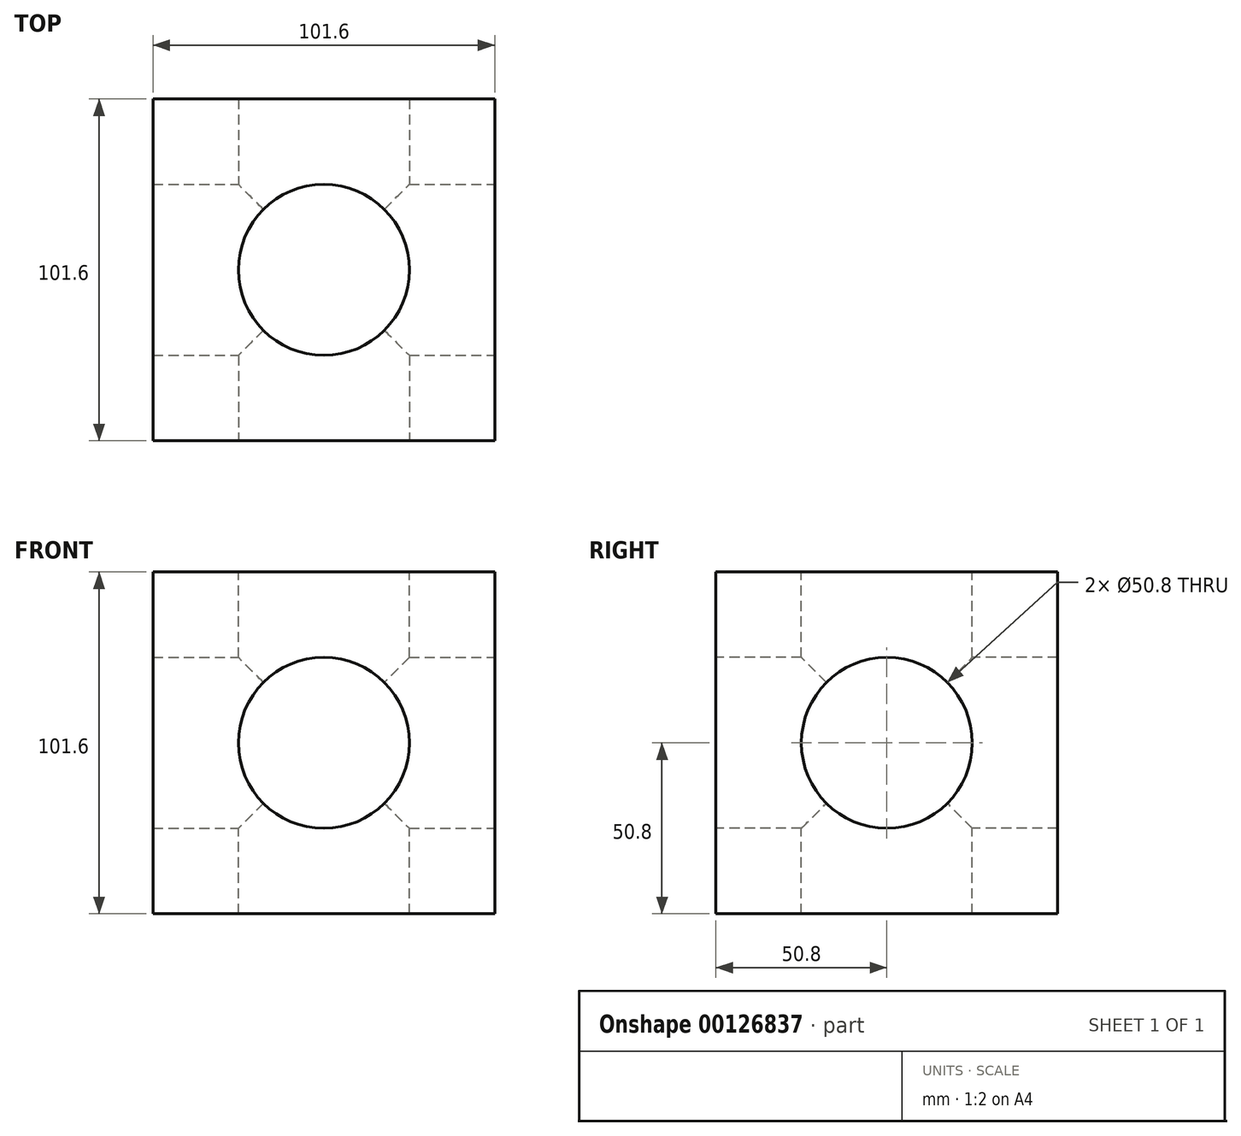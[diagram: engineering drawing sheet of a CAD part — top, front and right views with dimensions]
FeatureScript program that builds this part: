
annotation { "Feature Type Name" : "Feature", "Feature Type Description" : "" }
export const myFeature = defineFeature(function(context is Context, id is Id, definition is map)
    precondition{}
    {
        {
            var Q0;
            Q0=qCreatedBy(makeId("Front.planeOp"),FACE);
            var sketch = newSketch(context, id + "F0", { "sketchPlane" : qUnion([Q0])});
            skLineSegment(sketch, "E0", {"start": v(-50.8, -50.8) * mm, "end": v(-50.8, 50.8) * mm});
            skLineSegment(sketch, "E1", {"start": v(-50.8, 50.8) * mm, "end": v(50.8, 50.8) * mm});
            skLineSegment(sketch, "E2", {"start": v(50.8, 50.8) * mm, "end": v(50.8, -50.8) * mm});
            skLineSegment(sketch, "E3", {"start": v(50.8, -50.8) * mm, "end": v(-50.8, -50.8) * mm});
            skSolve(sketch);
        }
        {
            var Q0;
            Q0 = qSketchRegion(id + "F0", true);
            extrude(context, id + "F1", {"entities" : qUnion([Q0]), "endBound" : BoundingType.SYMMETRIC, "depth" : 101.6 * mm});
        }
        {
            var Q0;
            Q0=makeQuery(id+"F1.opExtrude","CAP_FACE",FACE,{"disambiguationData":[OSD([sQuery(id+"F0.wireOp",EDGE,"E0"),sQuery(id+"F0.wireOp",EDGE,"E1"),sQuery(id+"F0.wireOp",EDGE,"E2"),sQuery(id+"F0.wireOp",EDGE,"E3")])],"isStart":false});
            var sketch = newSketch(context, id + "F2", { "sketchPlane" : qUnion([Q0])});
            skCircle(sketch, "E4", {"center": v(0, 0) * mm, "radius": 25.4 * mm});
            skSolve(sketch);
        }
        {
            var Q0;
            Q0=makeQuery(id+"F2.imprint","IMPRINT",FACE,{"disambiguationData":[TD([[makeQuery(id+"F2.imprint","IMPRINT",EDGE,{"derivedFrom":sQuery(id+"F2.wireOp",EDGE,"E4")}),1.0]])]});
            extrude(context, id + "F3", {"entities" : qUnion([Q0]), "operationType" : NewBodyOperationType.REMOVE, "endBound" : BoundingType.THROUGH_ALL, "oppositeDirection" : true, "depth" : 25.4 * mm});
        }
        {
            var Q0;
            Q0=makeQuery(id+"F1.opExtrude","SWEPT_FACE",FACE,{"disambiguationData":[OSD([sQuery(id+"F0.wireOp",EDGE,"E1")])]});
            var sketch = newSketch(context, id + "F4", { "sketchPlane" : qUnion([Q0])});
            skCircle(sketch, "E5", {"center": v(0, 0) * mm, "radius": 25.4 * mm});
            skSolve(sketch);
        }
        {
            var Q0;
            Q0=makeQuery(id+"F4.imprint","IMPRINT",FACE,{"disambiguationData":[TD([[makeQuery(id+"F4.imprint","IMPRINT",EDGE,{"derivedFrom":sQuery(id+"F4.wireOp",EDGE,"E5")}),1.0]])]});
            extrude(context, id + "F5", {"entities" : qUnion([Q0]), "operationType" : NewBodyOperationType.REMOVE, "endBound" : BoundingType.THROUGH_ALL, "oppositeDirection" : true, "depth" : 25.4 * mm});
        }
        {
            var Q0;
            Q0=makeQuery(id+"F1.opExtrude","SWEPT_FACE",FACE,{"disambiguationData":[OSD([sQuery(id+"F0.wireOp",EDGE,"E2")])]});
            var sketch = newSketch(context, id + "F6", { "sketchPlane" : qUnion([Q0])});
            skCircle(sketch, "E6", {"center": v(0, 0) * mm, "radius": 25.4 * mm});
            skSolve(sketch);
        }
        {
            var Q0;
            Q0=makeQuery(id+"F6.imprint","IMPRINT",FACE,{"disambiguationData":[TD([[makeQuery(id+"F6.imprint","IMPRINT",EDGE,{"derivedFrom":sQuery(id+"F6.wireOp",EDGE,"E6")}),1.0]])]});
            extrude(context, id + "F7", {"entities" : qUnion([Q0]), "operationType" : NewBodyOperationType.REMOVE, "endBound" : BoundingType.THROUGH_ALL, "oppositeDirection" : true, "depth" : 25.4 * mm});
        }
    });
